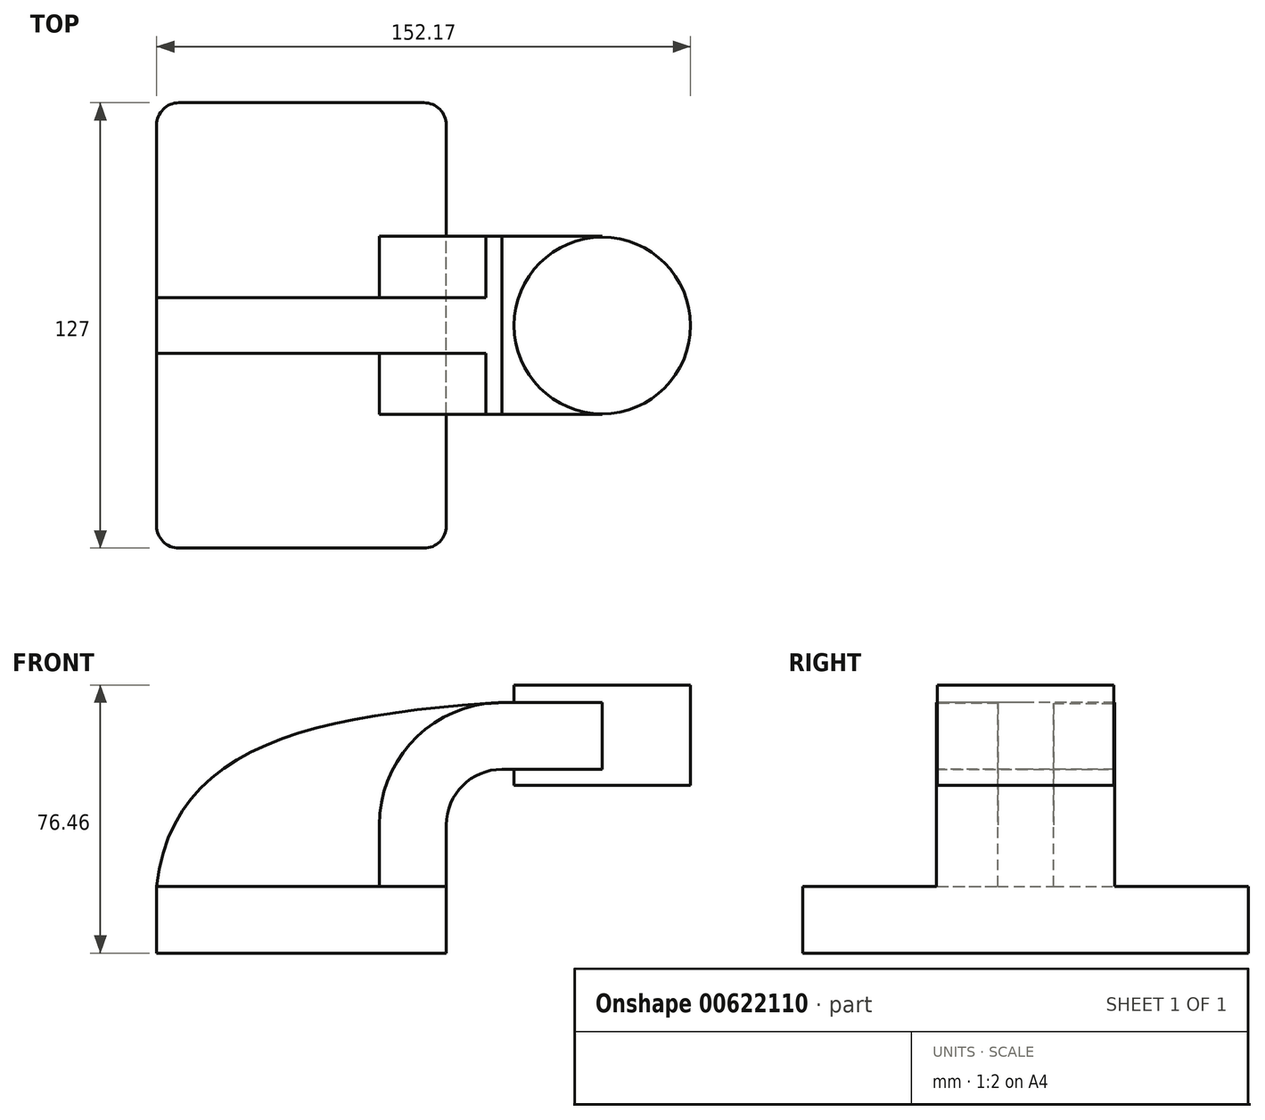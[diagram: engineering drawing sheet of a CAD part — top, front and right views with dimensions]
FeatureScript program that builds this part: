
annotation { "Feature Type Name" : "Feature", "Feature Type Description" : "" }
export const myFeature = defineFeature(function(context is Context, id is Id, definition is map)
    precondition{}
    {
        {
            var Q0;
            Q0=qCreatedBy(makeId("Front.planeOp"),FACE);
            var sketch = newSketch(context, id + "F0", { "sketchPlane" : qUnion([Q0])});
            skLineSegment(sketch, "E0.bottom", {"start": v(41.28, -9.52) * mm, "end": v(-41.28, -9.53) * mm});
            skLineSegment(sketch, "E0.top", {"start": v(41.28, 9.53) * mm, "end": v(-41.28, 9.53) * mm});
            skLineSegment(sketch, "E0.left", {"start": v(41.28, -9.52) * mm, "end": v(41.28, 9.53) * mm});
            skLineSegment(sketch, "E0.right", {"start": v(-41.28, -9.53) * mm, "end": v(-41.28, 9.53) * mm});
            skPoint(sketch, "E0.middle", {"position": v(0, 0) * mm});
            skLineSegment(sketch, "E1.bottom", {"start": v(110.9, 38.35) * mm, "end": v(60.1, 38.35) * mm});
            skLineSegment(sketch, "E1.top", {"start": v(110.9, 66.93) * mm, "end": v(60.1, 66.93) * mm});
            skLineSegment(sketch, "E1.left", {"start": v(110.9, 38.35) * mm, "end": v(110.9, 66.93) * mm});
            skLineSegment(sketch, "E1.right", {"start": v(60.1, 38.35) * mm, "end": v(60.1, 66.93) * mm});
            skPoint(sketch, "E1.middle", {"position": v(85.5, 52.64) * mm});
            skLineSegment(sketch, "E2", {"start": v(41.28, 9.53) * mm, "end": v(41.28, 27) * mm});
            skArc(sketch, "E3", {"start": v(41.27, 27) * mm, "mid": v(45.92, 38.23) * mm, "end": v(57.15, 42.88) * mm});
            skLineSegment(sketch, "E4", {"start": v(57.15, 42.88) * mm, "end": v(85.73, 42.88) * mm});
            skLineSegment(sketch, "E5.0", {"start": v(57.15, 61.93) * mm, "end": v(85.73, 61.93) * mm});
            skArc(sketch, "E5.1", {"start": v(22.23, 27) * mm, "mid": v(32.45, 51.7) * mm, "end": v(57.15, 61.93) * mm});
            skLineSegment(sketch, "E5.2", {"start": v(22.22, 9.53) * mm, "end": v(22.22, 27) * mm});
            skLineSegment(sketch, "E6", {"start": v(85.73, 38.35) * mm, "end": v(85.73, 66.93) * mm});
            skPoint(sketch, "E6.startSnap0", {"position": v(85.5, 38.35) * mm});
            skFitSpline(sketch, "E7", {"points": [v(-41.28, 9.53) * mm, v(57.15, 61.93) * mm], "startDerivative": vector(12.85, 120.35) * mm, "endDerivative": vector(162.65, 10.27) * mm});
            skSolve(sketch);
        }
        {
            var Q0;
            Q0=makeQuery(id+"F0.imprint","IMPRINT",FACE,{"disambiguationData":[TD([[makeQuery(id+"F0.imprint","IMPRINT",EDGE,{"derivedFrom":sQuery(id+"F0.wireOp",EDGE,"E0.bottom")}),-1.0]])]});
            extrude(context, id + "F1", {"entities" : qUnion([Q0]), "endBound" : BoundingType.SYMMETRIC, "depth" : 127 * mm, "offsetDistance" : 25.4 * mm});
        }
        {
            var Q0;
            {var subQ1=sQuery(id+"F0.wireOp",EDGE,"E2");Q0=makeQuery(id+"F0.imprint","IMPRINT",FACE,{"disambiguationData":[TD([[makeQuery(id+"F0.imprint","IMPRINT",EDGE,{"derivedFrom":subQ1}),1.0]])]});}
            var Q1;
            {var subQ0=sQuery(id+"F0.wireOp",EDGE,"E4");var subQ1=sQuery(id+"F0.wireOp",EDGE,"E1.right");var subQ2=makeQuery(id+"F0.imprint","INTERSECT",VERTEX,{"derivedFrom":[subQ1,subQ0]});Q1=makeQuery(id+"F0.imprint","IMPRINT",FACE,{"disambiguationData":[TD([[makeQuery(id+"F0.imprint","IMPRINT",EDGE,{"disambiguationData":[TD([[subQ2,-1.0]])],"derivedFrom":subQ1}),-1.0]])]});}
            extrude(context, id + "F2", {"entities" : qUnion([Q0, Q1]), "operationType" : NewBodyOperationType.ADD, "endBound" : BoundingType.SYMMETRIC, "depth" : 50.8 * mm, "offsetDistance" : 25.4 * mm});
        }
        {
            var Q0;
            {var subQ3=sQuery(id+"F0.wireOp",EDGE,"E5.2");Q0=makeQuery(id+"F0.imprint","IMPRINT",FACE,{"disambiguationData":[TD([[makeQuery(id+"F0.imprint","IMPRINT",EDGE,{"derivedFrom":subQ3}),1.0]])]});}
            extrude(context, id + "F3", {"entities" : qUnion([Q0]), "operationType" : NewBodyOperationType.ADD, "endBound" : BoundingType.SYMMETRIC, "depth" : 15.88 * mm, "offsetDistance" : 25.4 * mm});
        }
        {
            var Q0;
            {var subQ0=sQuery(id+"F0.wireOp",EDGE,"E1.left");Q0=makeQuery(id+"F0.imprint","IMPRINT",FACE,{"disambiguationData":[TD([[makeQuery(id+"F0.imprint","IMPRINT",EDGE,{"derivedFrom":subQ0}),1.0]])]});}
            var Q1;
            Q1=sQuery(id+"F0.wireOp",EDGE,"E6");
            revolve(context, id + "F4", {"operationType" : NewBodyOperationType.ADD, "entities" : qUnion([Q0]), "axis" : qUnion([Q1]), "revolveType" : RevolveType.FULL});
        }
        {
            var Q0;
            Q0=makeQuery(id+"F1.opExtrude","CAP_EDGE",EDGE,{"disambiguationData":[OSD([sQuery(id+"F0.wireOp",EDGE,"E0.right")])],"isStart":false});
            var Q1;
            Q1=makeQuery(id+"F1.opExtrude","CAP_EDGE",EDGE,{"disambiguationData":[OSD([sQuery(id+"F0.wireOp",EDGE,"E0.left")])],"isStart":false});
            var Q2;
            Q2=makeQuery(id+"F1.opExtrude","CAP_EDGE",EDGE,{"disambiguationData":[OSD([sQuery(id+"F0.wireOp",EDGE,"E0.right")])],"isStart":true});
            var Q3;
            Q3=makeQuery(id+"F1.opExtrude","CAP_EDGE",EDGE,{"disambiguationData":[OSD([sQuery(id+"F0.wireOp",EDGE,"E0.left")])],"isStart":true});
            fillet(context, id + "F5", {"entities" : qUnion([Q0, Q1, Q2, Q3]), "radius" : 6.35 * mm, "tangentPropagation" : true, "allowEdgeOverflow" : false});
        }
    });
